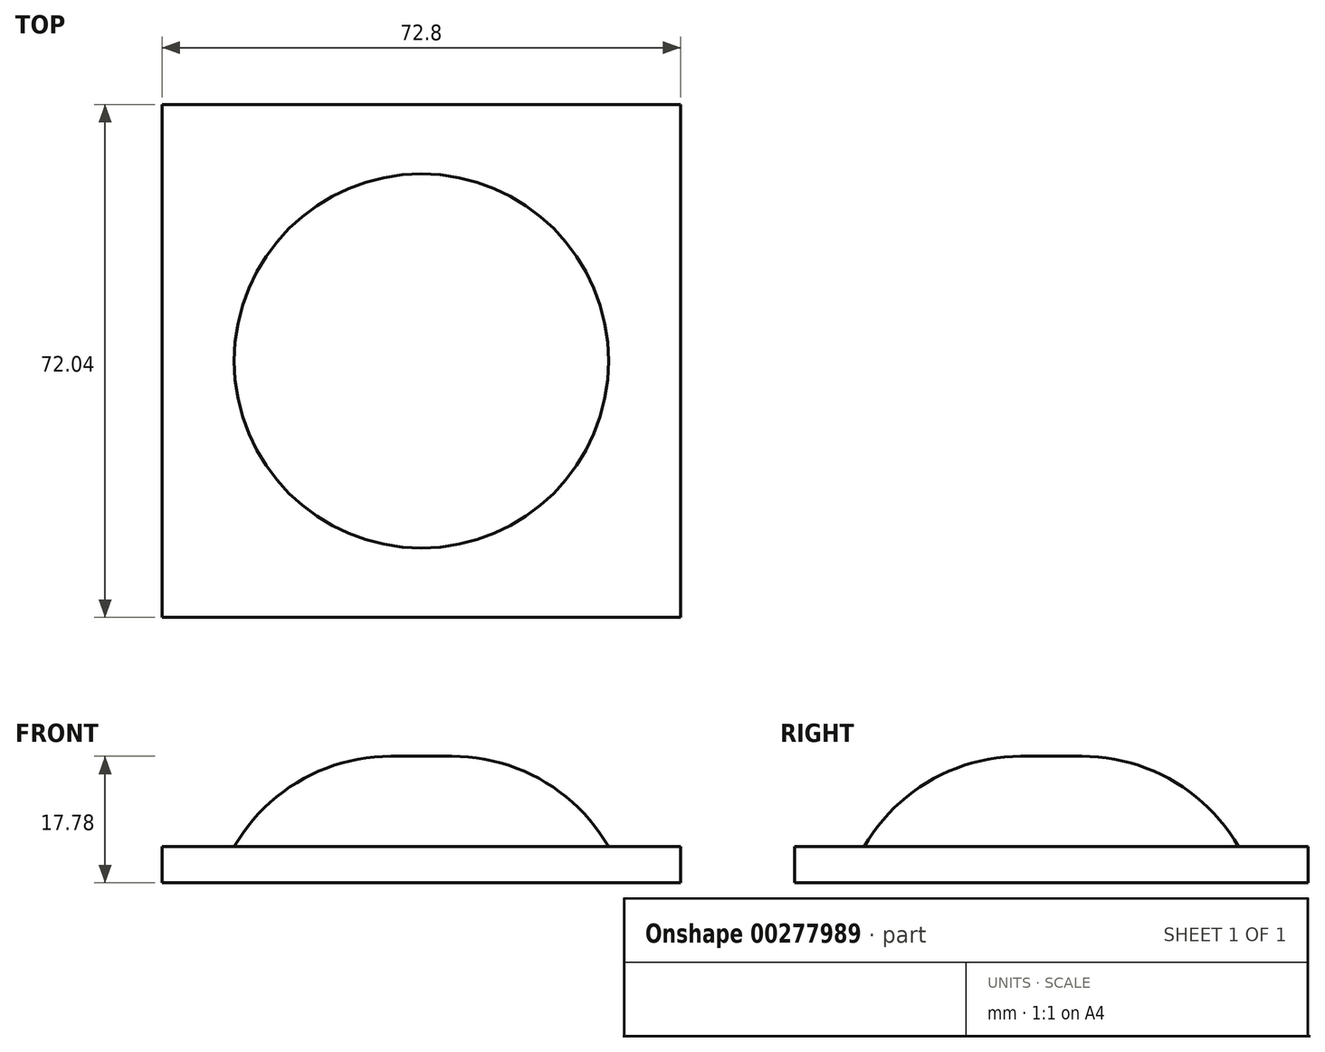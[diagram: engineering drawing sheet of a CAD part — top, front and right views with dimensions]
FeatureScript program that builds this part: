
annotation { "Feature Type Name" : "Feature", "Feature Type Description" : "" }
export const myFeature = defineFeature(function(context is Context, id is Id, definition is map)
    precondition{}
    {
        {
            var Q0;
            Q0=qCreatedBy(makeId("Top.planeOp"),FACE);
            var sketch = newSketch(context, id + "F0", { "sketchPlane" : qUnion([Q0])});
            skCircle(sketch, "E0", {"center": v(0, 0) * mm, "radius": 26.28 * mm});
            skSolve(sketch);
        }
        {
            var Q0;
            Q0=makeQuery(id+"F0.imprint","IMPRINT",FACE,{"disambiguationData":[TD([[makeQuery(id+"F0.imprint","IMPRINT",EDGE,{"derivedFrom":sQuery(id+"F0.wireOp",EDGE,"E0")}),1.0]])]});
            extrude(context, id + "F1", {"entities" : qUnion([Q0]), "depth" : 12.7 * mm});
        }
        {
            var Q0;
            Q0=makeQuery(id+"F1.opExtrude","CAP_EDGE",EDGE,{"disambiguationData":[OSD([sQuery(id+"F0.wireOp",EDGE,"E0")])],"isStart":false});
            fillet(context, id + "F2", {"entities" : qUnion([Q0]), "radius" : 25.4 * mm, "tangentPropagation" : true, "allowEdgeOverflow" : false});
        }
        {
            var Q0;
            Q0=qCreatedBy(makeId("Top.planeOp"),FACE);
            var sketch = newSketch(context, id + "F3", { "sketchPlane" : qUnion([Q0])});
            skLineSegment(sketch, "E1.bottom", {"start": v(36.4, 36.02) * mm, "end": v(-36.4, 36.02) * mm});
            skLineSegment(sketch, "E1.top", {"start": v(36.4, -36.02) * mm, "end": v(-36.4, -36.02) * mm});
            skLineSegment(sketch, "E1.left", {"start": v(36.4, 36.02) * mm, "end": v(36.4, -36.02) * mm});
            skLineSegment(sketch, "E1.right", {"start": v(-36.4, 36.02) * mm, "end": v(-36.4, -36.02) * mm});
            skPoint(sketch, "E1.middle", {"position": v(0, 0) * mm});
            skSolve(sketch);
        }
        {
            var Q0;
            Q0 = qSketchRegion(id + "F3", true);
            extrude(context, id + "F4", {"entities" : qUnion([Q0]), "operationType" : NewBodyOperationType.ADD, "oppositeDirection" : true, "depth" : 5.08 * mm});
        }
    });
